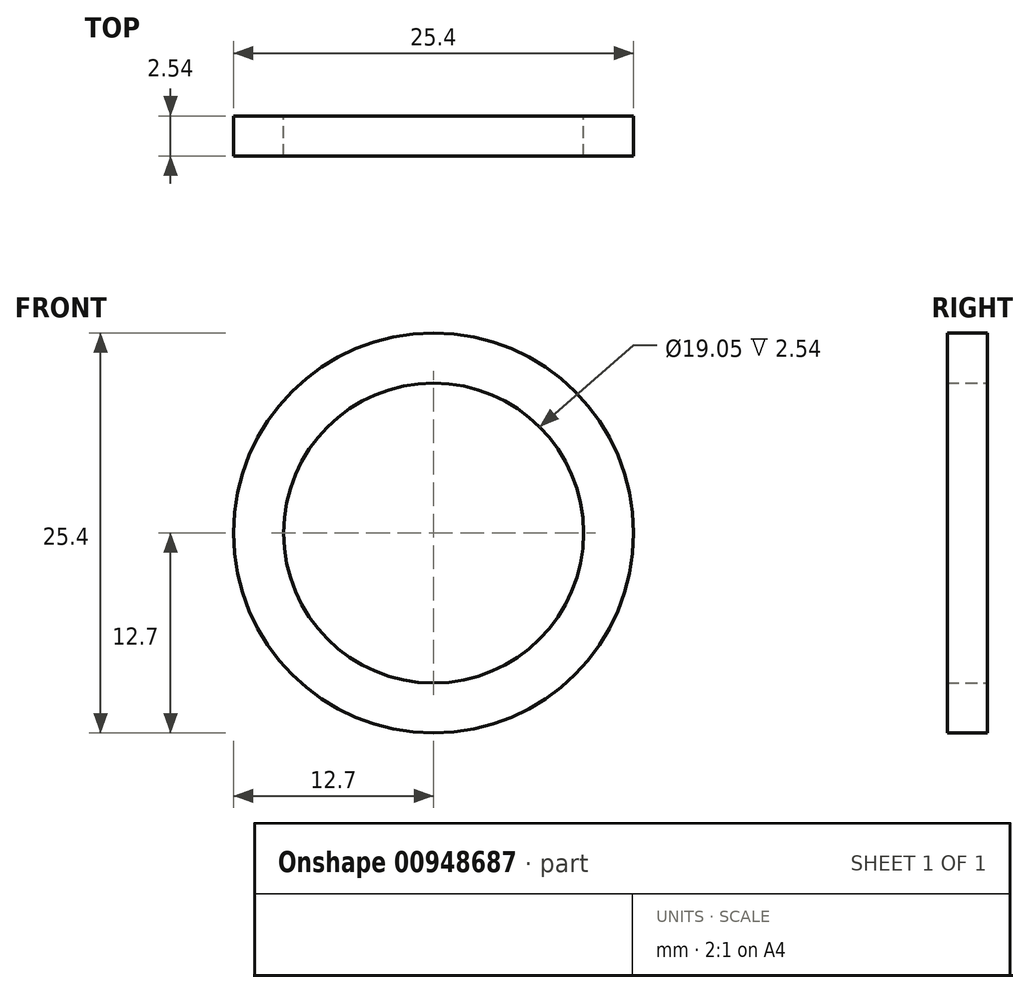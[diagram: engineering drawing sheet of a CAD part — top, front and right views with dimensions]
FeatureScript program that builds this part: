
annotation { "Feature Type Name" : "Feature", "Feature Type Description" : "" }
export const myFeature = defineFeature(function(context is Context, id is Id, definition is map)
    precondition{}
    {
        {
            var Q0;
            Q0=qCreatedBy(makeId("Front.planeOp"),FACE);
            var sketch = newSketch(context, id + "F0", { "sketchPlane" : qUnion([Q0])});
            skCircle(sketch, "E0", {"center": v(0, 0) * mm, "radius": 9.53 * mm});
            skCircle(sketch, "E1", {"center": v(0, 0) * mm, "radius": 12.7 * mm});
            skSolve(sketch);
        }
        {
            var Q0;
            Q0=makeQuery(id+"F0.imprint","IMPRINT",FACE,{"disambiguationData":[TD([[makeQuery(id+"F0.imprint","IMPRINT",EDGE,{"derivedFrom":sQuery(id+"F0.wireOp",EDGE,"E0")}),-1.0]])]});
            extrude(context, id + "F1", {"entities" : qUnion([Q0]), "depth" : 2.54 * mm, "offsetDistance" : 25.4 * mm});
        }
    });
